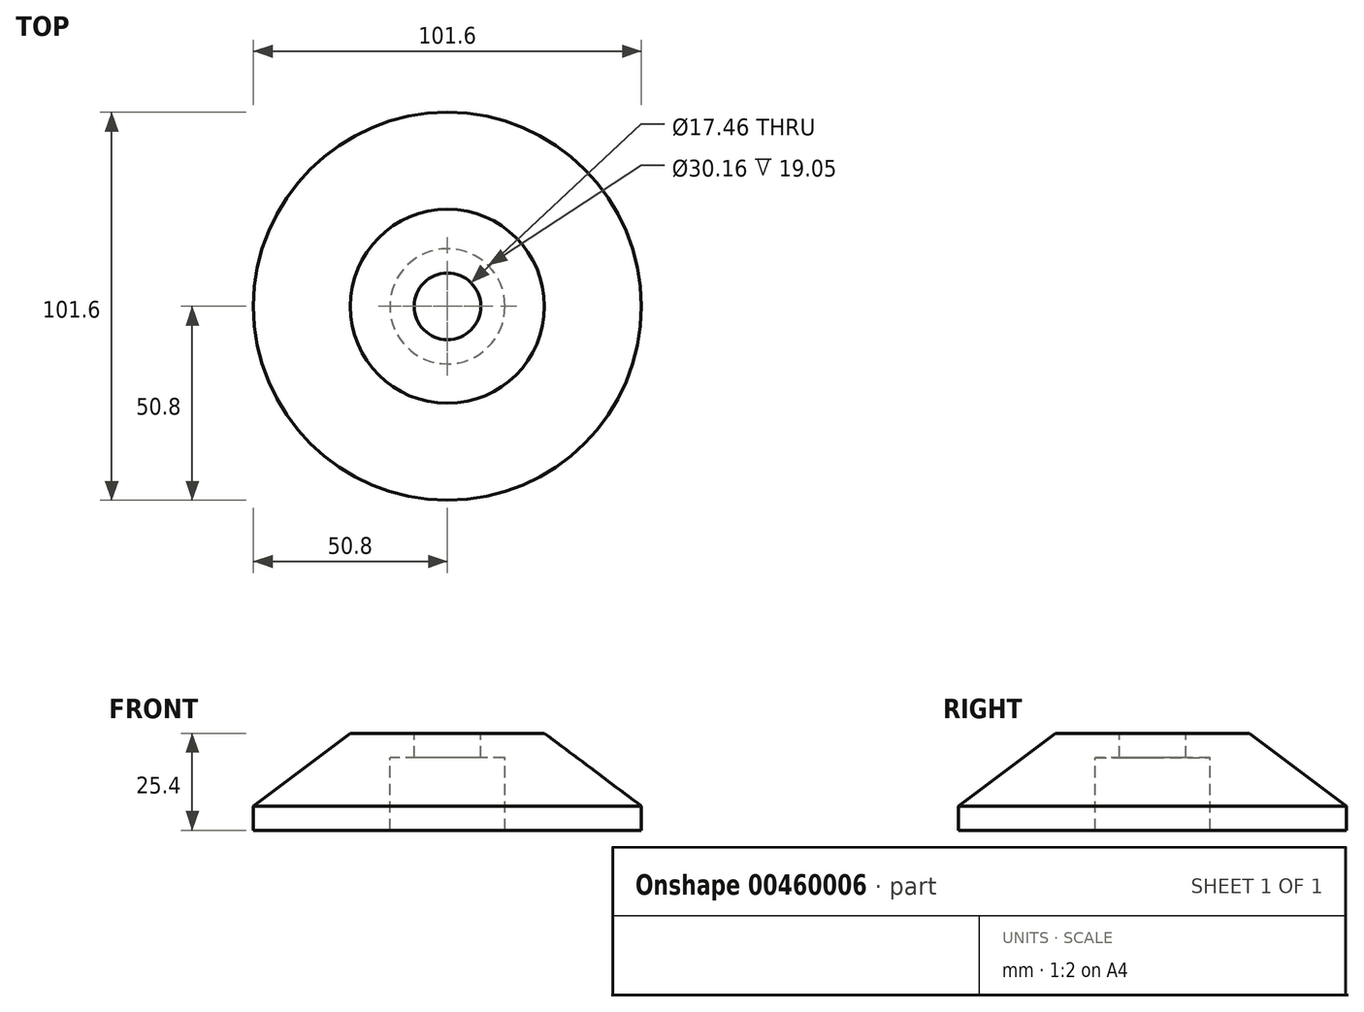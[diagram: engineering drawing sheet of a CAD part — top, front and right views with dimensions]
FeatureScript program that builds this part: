
annotation { "Feature Type Name" : "Feature", "Feature Type Description" : "" }
export const myFeature = defineFeature(function(context is Context, id is Id, definition is map)
    precondition{}
    {
        {
            var Q0;
            Q0=qCreatedBy(makeId("Top.planeOp"),FACE);
            var sketch = newSketch(context, id + "F0", { "sketchPlane" : qUnion([Q0])});
            skCircle(sketch, "E0", {"center": v(0, 0) * mm, "radius": 50.8 * mm});
            skSolve(sketch);
        }
        {
            var Q0;
            Q0=qSketchRegion(id+"F0",true);
            extrude(context, id + "F1", {"entities" : qUnion([Q0]), "depth" : 6.35 * mm});
        }
        {
            var Q0;
            Q0=makeQuery(id+"F1.opExtrude","CAP_FACE",FACE,{"disambiguationData":[OSD([sQuery(id+"F0.wireOp",EDGE,"E0")])],"isStart":false});
            cPlane(context, id + "F2", {"entities" : qUnion([Q0]), "cplaneType" : CPlaneType.OFFSET, "offset" : 19.05 * mm, "width" : 152.4 * mm, "height" : 152.4 * mm});
        }
        {
            var Q0;
            Q0=qCreatedBy(id+"F2.planeOp",FACE);
            var sketch = newSketch(context, id + "F3", { "sketchPlane" : qUnion([Q0])});
            skCircle(sketch, "E1", {"center": v(0, 0) * mm, "radius": 25.4 * mm});
            skSolve(sketch);
        }
        {
            var Q1;
            Q1=makeQuery(id+"F3.imprint","IMPRINT",FACE,{"disambiguationData":[TD([[makeQuery(id+"F3.imprint","IMPRINT",EDGE,{"derivedFrom":sQuery(id+"F3.wireOp",EDGE,"E1")}),1.0]])]});
            var Q2;
            Q2=makeQuery(id+"F1.opExtrude","CAP_FACE",FACE,{"disambiguationData":[OSD([sQuery(id+"F0.wireOp",EDGE,"E0")])],"isStart":false});
            loft(context, id + "F4", {"operationType" : NewBodyOperationType.ADD, "sheetProfilesArray" : [{ "sheetProfileEntities" : qUnion([Q1]) }, { "sheetProfileEntities" : qUnion([Q2]) }]});
        }
        {
            var Q0;
            Q0=makeQuery(id+"F1.opExtrude","CAP_FACE",FACE,{"disambiguationData":[OSD([sQuery(id+"F0.wireOp",EDGE,"E0")])],"isStart":true});
            var sketch = newSketch(context, id + "F5", { "sketchPlane" : qUnion([Q0])});
            skPoint(sketch, "E2", {"position": v(0, 0) * mm});
            skSolve(sketch);
        }
        {
            var Q0;
            Q0=sQuery(id+"F5.wireOp",VERTEX,"E2");
            var Q1;
            Q1=makeQuery(id+"F1.opExtrude","SWEPT_BODY",BODY,{"disambiguationData":[OSD([sQuery(id+"F0.wireOp",EDGE,"E0")])]});
            hole(context, id + "F6", {"style" : HoleStyle.C_BORE, "endStyle" : HoleEndStyle.THROUGH, "standardTappedOrClearance" : lookupTablePath({ "standard" : "ANSI", "engagement" : "50%", "pitch" : "10 tpi", "size" : "3/4", "type" : "Tapped" }), "standardBlindInLast" : lookupTablePath({ "standard" : "ANSI", "engagement" : "50%", "pitch" : "10 tpi", "size" : "3/4", "type" : "Tapped" }), "holeDiameter" : 17.46 * mm, "cBoreDiameter" : 30.16 * mm, "cBoreDepth" : 19.05 * mm, "showTappedDepth" : true, "tappedDepth" : 14.27 * mm, "tapClearance" : 3, "locations" : qUnion([Q0]), "scope" : qUnion([Q1]), "majorDiameter" : 19.05 * mm, "startStyle" : HoleStartStyle.PART});
        }
    });
